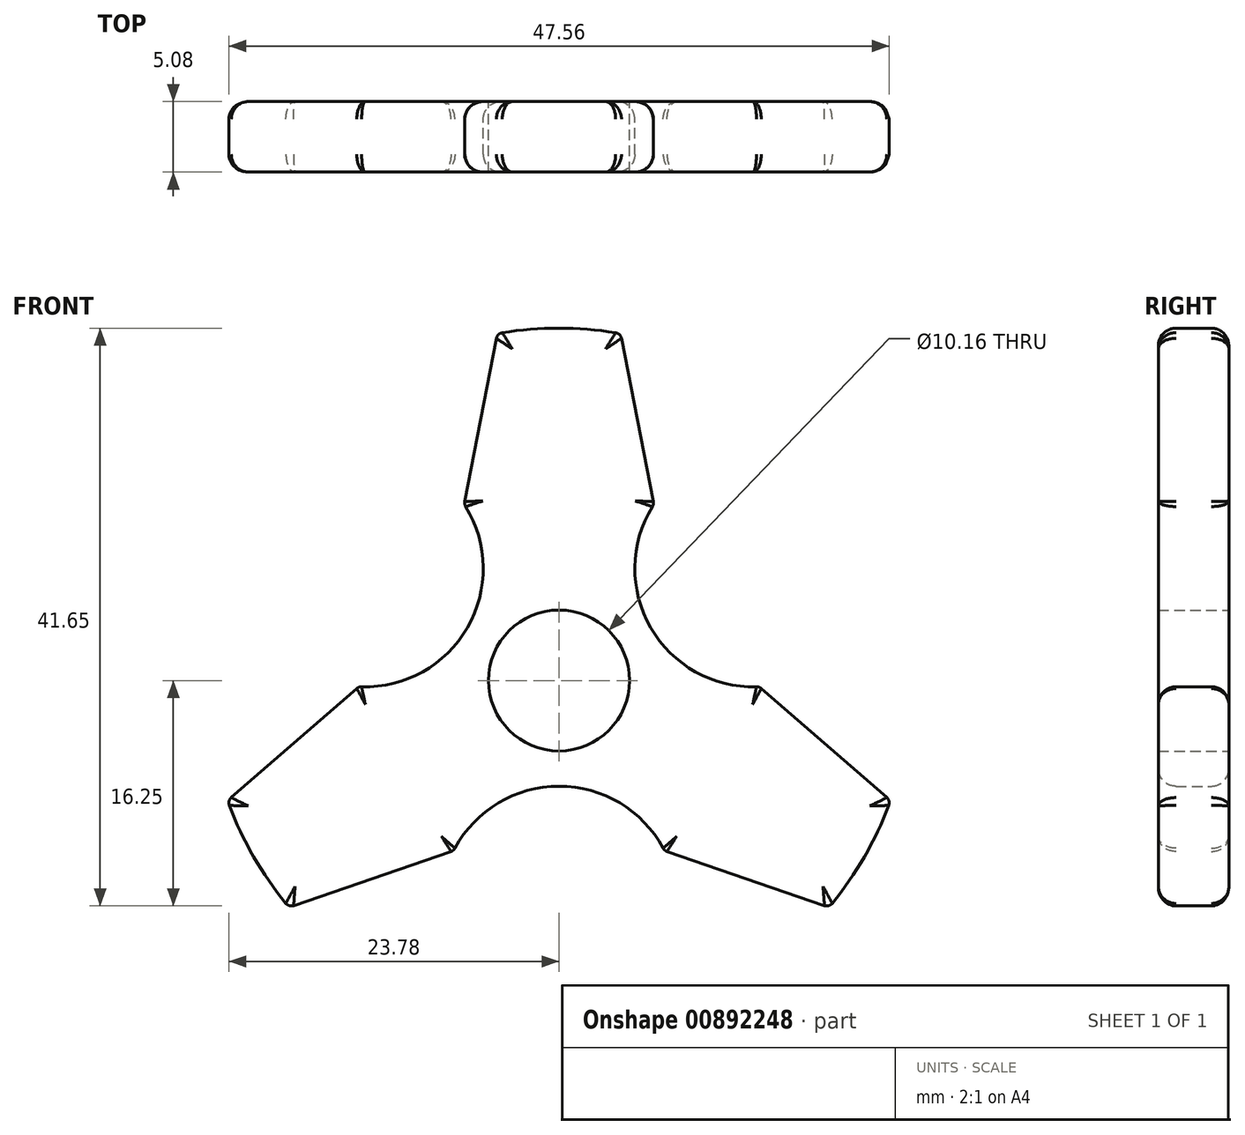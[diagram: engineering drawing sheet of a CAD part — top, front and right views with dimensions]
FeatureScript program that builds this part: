
annotation { "Feature Type Name" : "Feature", "Feature Type Description" : "" }
export const myFeature = defineFeature(function(context is Context, id is Id, definition is map)
    precondition{}
    {
        {
            var Q0;
            Q0=qCreatedBy(makeId("Front.planeOp"),FACE);
            var sketch = newSketch(context, id + "F0", { "sketchPlane" : qUnion([Q0])});
            skCircle(sketch, "E0", {"center": v(0, 0) * mm, "radius": 7.62 * mm});
            skCircle(sketch, "E1", {"center": v(0, 0) * mm, "radius": 25.4 * mm});
            skLineSegment(sketch, "E2", {"start": v(0, 25.4) * mm, "end": v(0, 0) * mm});
            skLineSegment(sketch, "E3", {"start": v(0, 0) * mm, "end": v(-22, -12.7) * mm});
            skLineSegment(sketch, "E4", {"start": v(0, 0) * mm, "end": v(22, -12.7) * mm});
            skPoint(sketch, "E5", {"position": v(-23.87, -8.67) * mm});
            skPoint(sketch, "E6", {"position": v(-19.45, -16.34) * mm});
            skPoint(sketch, "E7", {"position": v(19.45, -16.34) * mm});
            skPoint(sketch, "E8", {"position": v(23.87, -8.67) * mm});
            skPoint(sketch, "E9", {"position": v(4.43, 25.01) * mm});
            skPoint(sketch, "E10", {"position": v(-4.45, 25) * mm});
            skPoint(sketch, "E11", {"position": v(0, 7.62) * mm});
            skPoint(sketch, "E12", {"position": v(-6.6, -3.8) * mm});
            skPoint(sketch, "E13", {"position": v(6.6, -3.8) * mm});
            skLineSegment(sketch, "E14", {"start": v(0, 7.62) * mm, "end": v(-6.83, 12.7) * mm});
            skLineSegment(sketch, "E15", {"start": v(0, 7.62) * mm, "end": v(6.83, 12.7) * mm});
            skLineSegment(sketch, "E16", {"start": v(-4.44, 25) * mm, "end": v(-6.83, 12.7) * mm});
            skLineSegment(sketch, "E17", {"start": v(4.43, 25.01) * mm, "end": v(6.83, 12.7) * mm});
            skLineSegment(sketch, "E18", {"start": v(-6.6, -3.8) * mm, "end": v(-7.6, -12.26) * mm});
            skLineSegment(sketch, "E19", {"start": v(-6.6, -3.8) * mm, "end": v(-14.41, -0.44) * mm});
            skLineSegment(sketch, "E20", {"start": v(6.6, -3.8) * mm, "end": v(7.6, -12.26) * mm});
            skLineSegment(sketch, "E21", {"start": v(6.6, -3.8) * mm, "end": v(14.41, -0.44) * mm});
            skLineSegment(sketch, "E22", {"start": v(14.41, -0.44) * mm, "end": v(23.87, -8.67) * mm});
            skLineSegment(sketch, "E23", {"start": v(7.6, -12.26) * mm, "end": v(19.45, -16.34) * mm});
            skLineSegment(sketch, "E24", {"start": v(-7.6, -12.26) * mm, "end": v(-19.45, -16.34) * mm});
            skLineSegment(sketch, "E25", {"start": v(-14.41, -0.44) * mm, "end": v(-23.87, -8.67) * mm});
            skCircle(sketch, "E26", {"center": v(-13.98, 8.07) * mm, "radius": 8.52 * mm});
            skCircle(sketch, "E27", {"center": v(13.98, 8.07) * mm, "radius": 8.52 * mm});
            skCircle(sketch, "E28", {"center": v(0, -16.15) * mm, "radius": 8.53 * mm});
            skCircle(sketch, "E29", {"center": v(0, 0) * mm, "radius": 5.08 * mm});
            skSolve(sketch);
        }
        {
            var Q0;
            {var subQ4=sQuery(id+"F0.wireOp",EDGE,"E15");Q0=makeQuery(id+"F0.imprint","IMPRINT",FACE,{"disambiguationData":[TD([[makeQuery(id+"F0.imprint","IMPRINT",EDGE,{"derivedFrom":subQ4}),1.0]])]});}
            var Q1;
            {var subQ4=sQuery(id+"F0.wireOp",EDGE,"E14");Q1=makeQuery(id+"F0.imprint","IMPRINT",FACE,{"disambiguationData":[TD([[makeQuery(id+"F0.imprint","IMPRINT",EDGE,{"derivedFrom":subQ4}),-1.0]])]});}
            var Q2;
            {var subQ0=sQuery(id+"F0.wireOp",EDGE,"E14");Q2=makeQuery(id+"F0.imprint","IMPRINT",FACE,{"disambiguationData":[TD([[makeQuery(id+"F0.imprint","IMPRINT",EDGE,{"derivedFrom":subQ0}),1.0]])]});}
            var Q3;
            {var subQ0=sQuery(id+"F0.wireOp",EDGE,"E15");Q3=makeQuery(id+"F0.imprint","IMPRINT",FACE,{"disambiguationData":[TD([[makeQuery(id+"F0.imprint","IMPRINT",EDGE,{"derivedFrom":subQ0}),-1.0]])]});}
            var Q4;
            {var subQ1=sQuery(id+"F0.wireOp",EDGE,"E0");var subQ3=makeQuery(id+"F0.imprint","INTERSECT",VERTEX,{"derivedFrom":[subQ1,sQuery(id+"F0.wireOp",EDGE,"E27")]});Q4=makeQuery(id+"F0.imprint","IMPRINT",FACE,{"disambiguationData":[TD([[makeQuery(id+"F0.imprint","IMPRINT",EDGE,{"disambiguationData":[TD([[subQ3,-1.0]])],"derivedFrom":subQ1}),1.0]])]});}
            var Q5;
            {var subQ1=sQuery(id+"F0.wireOp",EDGE,"E0");var subQ3=makeQuery(id+"F0.imprint","INTERSECT",VERTEX,{"derivedFrom":[subQ1,sQuery(id+"F0.wireOp",EDGE,"E26")]});Q5=makeQuery(id+"F0.imprint","IMPRINT",FACE,{"disambiguationData":[TD([[makeQuery(id+"F0.imprint","IMPRINT",EDGE,{"disambiguationData":[TD([[subQ3,1.0]])],"derivedFrom":subQ1}),1.0]])]});}
            var Q6;
            {var subQ0=sQuery(id+"F0.wireOp",EDGE,"E19");Q6=makeQuery(id+"F0.imprint","IMPRINT",FACE,{"disambiguationData":[TD([[makeQuery(id+"F0.imprint","IMPRINT",EDGE,{"derivedFrom":subQ0}),-1.0]])]});}
            var Q7;
            {var subQ4=sQuery(id+"F0.wireOp",EDGE,"E19");Q7=makeQuery(id+"F0.imprint","IMPRINT",FACE,{"disambiguationData":[TD([[makeQuery(id+"F0.imprint","IMPRINT",EDGE,{"derivedFrom":subQ4}),1.0]])]});}
            var Q8;
            {var subQ4=sQuery(id+"F0.wireOp",EDGE,"E18");Q8=makeQuery(id+"F0.imprint","IMPRINT",FACE,{"disambiguationData":[TD([[makeQuery(id+"F0.imprint","IMPRINT",EDGE,{"derivedFrom":subQ4}),-1.0]])]});}
            var Q9;
            {var subQ0=sQuery(id+"F0.wireOp",EDGE,"E18");Q9=makeQuery(id+"F0.imprint","IMPRINT",FACE,{"disambiguationData":[TD([[makeQuery(id+"F0.imprint","IMPRINT",EDGE,{"derivedFrom":subQ0}),1.0]])]});}
            var Q10;
            {var subQ1=sQuery(id+"F0.wireOp",EDGE,"E0");var subQ3=makeQuery(id+"F0.imprint","INTERSECT",VERTEX,{"derivedFrom":[subQ1,sQuery(id+"F0.wireOp",EDGE,"E28")]});Q10=makeQuery(id+"F0.imprint","IMPRINT",FACE,{"disambiguationData":[TD([[makeQuery(id+"F0.imprint","IMPRINT",EDGE,{"disambiguationData":[TD([[subQ3,1.0]])],"derivedFrom":subQ1}),1.0]])]});}
            var Q11;
            {var subQ4=sQuery(id+"F0.wireOp",EDGE,"E20");Q11=makeQuery(id+"F0.imprint","IMPRINT",FACE,{"disambiguationData":[TD([[makeQuery(id+"F0.imprint","IMPRINT",EDGE,{"derivedFrom":subQ4}),1.0]])]});}
            var Q12;
            {var subQ0=sQuery(id+"F0.wireOp",EDGE,"E20");Q12=makeQuery(id+"F0.imprint","IMPRINT",FACE,{"disambiguationData":[TD([[makeQuery(id+"F0.imprint","IMPRINT",EDGE,{"derivedFrom":subQ0}),-1.0]])]});}
            var Q13;
            {var subQ0=sQuery(id+"F0.wireOp",EDGE,"E21");Q13=makeQuery(id+"F0.imprint","IMPRINT",FACE,{"disambiguationData":[TD([[makeQuery(id+"F0.imprint","IMPRINT",EDGE,{"derivedFrom":subQ0}),1.0]])]});}
            var Q14;
            {var subQ4=sQuery(id+"F0.wireOp",EDGE,"E21");Q14=makeQuery(id+"F0.imprint","IMPRINT",FACE,{"disambiguationData":[TD([[makeQuery(id+"F0.imprint","IMPRINT",EDGE,{"derivedFrom":subQ4}),-1.0]])]});}
            extrude(context, id + "F1", {"entities" : qUnion([Q0, Q1, Q2, Q3, Q4, Q5, Q6, Q7, Q8, Q9, Q10, Q11, Q12, Q13, Q14]), "endBound" : BoundingType.SYMMETRIC, "depth" : 5.08 * mm, "offsetDistance" : 25.4 * mm});
        }
        {
            var Q0;
            Q0=makeQuery(id+"F1.opExtrude","CAP_EDGE",EDGE,{"disambiguationData":[OSD([sQuery(id+"F0.wireOp",EDGE,"E17")])],"isStart":false});
            var Q1;
            Q1=makeQuery(id+"F1.opExtrude","CAP_EDGE",EDGE,{"disambiguationData":[OSD([sQuery(id+"F0.wireOp",EDGE,"E22")])],"isStart":false});
            var Q2;
            Q2=makeQuery(id+"F1.opExtrude","CAP_EDGE",EDGE,{"disambiguationData":[OSD([sQuery(id+"F0.wireOp",EDGE,"E27")])],"isStart":false});
            var Q3;
            Q3=makeQuery(id+"F1.opExtrude","CAP_EDGE",EDGE,{"disambiguationData":[OSD([sQuery(id+"F0.wireOp",EDGE,"E23")])],"isStart":false});
            var Q4;
            {var subQ0=sQuery(id+"F0.wireOp",EDGE,"E1");var subQ1=makeQuery(id+"F0.imprint","INTERSECT",VERTEX,{"derivedFrom":[subQ0,sQuery(id+"F0.wireOp",EDGE,"E4")]});Q4=makeQuery(id+"F1.opExtrude","CAP_EDGE",EDGE,{"disambiguationData":[OSD([subQ0]),TDD([makeQuery(id+"F0.imprint","IMPRINT",EDGE,{"disambiguationData":[TD([[subQ1,1.0]])],"derivedFrom":subQ0}),makeQuery(id+"F0.imprint","IMPRINT",EDGE,{"disambiguationData":[TD([[subQ1,-1.0]])],"derivedFrom":subQ0})])],"isStart":false});}
            var Q5;
            Q5=makeQuery(id+"F1.opExtrude","CAP_EDGE",EDGE,{"disambiguationData":[OSD([sQuery(id+"F0.wireOp",EDGE,"E28")])],"isStart":false});
            var Q6;
            Q6=makeQuery(id+"F1.opExtrude","CAP_EDGE",EDGE,{"disambiguationData":[OSD([sQuery(id+"F0.wireOp",EDGE,"E24")])],"isStart":false});
            var Q7;
            {var subQ0=sQuery(id+"F0.wireOp",EDGE,"E1");var subQ1=makeQuery(id+"F0.imprint","INTERSECT",VERTEX,{"derivedFrom":[subQ0,sQuery(id+"F0.wireOp",EDGE,"E3")]});Q7=makeQuery(id+"F1.opExtrude","CAP_EDGE",EDGE,{"disambiguationData":[OSD([subQ0]),TDD([makeQuery(id+"F0.imprint","IMPRINT",EDGE,{"disambiguationData":[TD([[subQ1,1.0]])],"derivedFrom":subQ0}),makeQuery(id+"F0.imprint","IMPRINT",EDGE,{"disambiguationData":[TD([[subQ1,-1.0]])],"derivedFrom":subQ0})])],"isStart":false});}
            var Q8;
            Q8=makeQuery(id+"F1.opExtrude","CAP_EDGE",EDGE,{"disambiguationData":[OSD([sQuery(id+"F0.wireOp",EDGE,"E25")])],"isStart":false});
            var Q9;
            Q9=makeQuery(id+"F1.opExtrude","CAP_EDGE",EDGE,{"disambiguationData":[OSD([sQuery(id+"F0.wireOp",EDGE,"E26")])],"isStart":false});
            var Q10;
            Q10=makeQuery(id+"F1.opExtrude","CAP_EDGE",EDGE,{"disambiguationData":[OSD([sQuery(id+"F0.wireOp",EDGE,"E16")])],"isStart":false});
            var Q11;
            {var subQ0=sQuery(id+"F0.wireOp",EDGE,"E1");var subQ1=makeQuery(id+"F0.imprint","INTERSECT",VERTEX,{"derivedFrom":[subQ0,sQuery(id+"F0.wireOp",EDGE,"E2")]});Q11=makeQuery(id+"F1.opExtrude","CAP_EDGE",EDGE,{"disambiguationData":[OSD([subQ0]),TDD([makeQuery(id+"F0.imprint","IMPRINT",EDGE,{"disambiguationData":[TD([[subQ1,1.0]])],"derivedFrom":subQ0}),makeQuery(id+"F0.imprint","IMPRINT",EDGE,{"disambiguationData":[TD([[subQ1,-1.0]])],"derivedFrom":subQ0})])],"isStart":false});}
            fillet(context, id + "F2", {"entities" : qUnion([Q0, Q1, Q2, Q3, Q4, Q5, Q6, Q7, Q8, Q9, Q10, Q11]), "radius" : 1.27 * mm, "tangentPropagation" : true, "allowEdgeOverflow" : false});
        }
        {
            var Q0;
            Q0=makeQuery(id+"F1.opExtrude","CAP_EDGE",EDGE,{"disambiguationData":[OSD([sQuery(id+"F0.wireOp",EDGE,"E24")])],"isStart":true});
            var Q1;
            Q1=makeQuery(id+"F1.opExtrude","CAP_EDGE",EDGE,{"disambiguationData":[OSD([sQuery(id+"F0.wireOp",EDGE,"E28")])],"isStart":true});
            var Q2;
            Q2=makeQuery(id+"F1.opExtrude","CAP_EDGE",EDGE,{"disambiguationData":[OSD([sQuery(id+"F0.wireOp",EDGE,"E23")])],"isStart":true});
            var Q3;
            {var subQ0=sQuery(id+"F0.wireOp",EDGE,"E1");var subQ1=makeQuery(id+"F0.imprint","INTERSECT",VERTEX,{"derivedFrom":[subQ0,sQuery(id+"F0.wireOp",EDGE,"E4")]});Q3=makeQuery(id+"F1.opExtrude","CAP_EDGE",EDGE,{"disambiguationData":[OSD([subQ0]),TDD([makeQuery(id+"F0.imprint","IMPRINT",EDGE,{"disambiguationData":[TD([[subQ1,1.0]])],"derivedFrom":subQ0}),makeQuery(id+"F0.imprint","IMPRINT",EDGE,{"disambiguationData":[TD([[subQ1,-1.0]])],"derivedFrom":subQ0})])],"isStart":true});}
            var Q4;
            Q4=makeQuery(id+"F1.opExtrude","CAP_EDGE",EDGE,{"disambiguationData":[OSD([sQuery(id+"F0.wireOp",EDGE,"E22")])],"isStart":true});
            var Q5;
            Q5=makeQuery(id+"F1.opExtrude","CAP_EDGE",EDGE,{"disambiguationData":[OSD([sQuery(id+"F0.wireOp",EDGE,"E27")])],"isStart":true});
            var Q6;
            Q6=makeQuery(id+"F1.opExtrude","CAP_EDGE",EDGE,{"disambiguationData":[OSD([sQuery(id+"F0.wireOp",EDGE,"E17")])],"isStart":true});
            var Q7;
            {var subQ0=sQuery(id+"F0.wireOp",EDGE,"E1");var subQ1=makeQuery(id+"F0.imprint","INTERSECT",VERTEX,{"derivedFrom":[subQ0,sQuery(id+"F0.wireOp",EDGE,"E2")]});Q7=makeQuery(id+"F1.opExtrude","CAP_EDGE",EDGE,{"disambiguationData":[OSD([subQ0]),TDD([makeQuery(id+"F0.imprint","IMPRINT",EDGE,{"disambiguationData":[TD([[subQ1,1.0]])],"derivedFrom":subQ0}),makeQuery(id+"F0.imprint","IMPRINT",EDGE,{"disambiguationData":[TD([[subQ1,-1.0]])],"derivedFrom":subQ0})])],"isStart":true});}
            var Q8;
            Q8=makeQuery(id+"F1.opExtrude","CAP_EDGE",EDGE,{"disambiguationData":[OSD([sQuery(id+"F0.wireOp",EDGE,"E16")])],"isStart":true});
            var Q9;
            Q9=makeQuery(id+"F1.opExtrude","CAP_EDGE",EDGE,{"disambiguationData":[OSD([sQuery(id+"F0.wireOp",EDGE,"E26")])],"isStart":true});
            var Q10;
            Q10=makeQuery(id+"F1.opExtrude","CAP_EDGE",EDGE,{"disambiguationData":[OSD([sQuery(id+"F0.wireOp",EDGE,"E25")])],"isStart":true});
            var Q11;
            {var subQ0=sQuery(id+"F0.wireOp",EDGE,"E1");var subQ1=makeQuery(id+"F0.imprint","INTERSECT",VERTEX,{"derivedFrom":[subQ0,sQuery(id+"F0.wireOp",EDGE,"E3")]});Q11=makeQuery(id+"F1.opExtrude","CAP_EDGE",EDGE,{"disambiguationData":[OSD([subQ0]),TDD([makeQuery(id+"F0.imprint","IMPRINT",EDGE,{"disambiguationData":[TD([[subQ1,1.0]])],"derivedFrom":subQ0}),makeQuery(id+"F0.imprint","IMPRINT",EDGE,{"disambiguationData":[TD([[subQ1,-1.0]])],"derivedFrom":subQ0})])],"isStart":true});}
            fillet(context, id + "F3", {"entities" : qUnion([Q0, Q1, Q2, Q3, Q4, Q5, Q6, Q7, Q8, Q9, Q10, Q11]), "radius" : 1.27 * mm, "tangentPropagation" : true, "allowEdgeOverflow" : false});
        }
        {
            var Q0;
            Q0=makeQuery(id+"F1.opExtrude","SWEPT_EDGE",EDGE,{"disambiguationData":[OSD([sQuery(id+"F0.wireOp",EDGE,"E1"),sQuery(id+"F0.wireOp",EDGE,"E16")])]});
            var Q1;
            Q1=makeQuery(id+"F1.opExtrude","SWEPT_EDGE",EDGE,{"disambiguationData":[OSD([sQuery(id+"F0.wireOp",EDGE,"E14"),sQuery(id+"F0.wireOp",EDGE,"E16"),sQuery(id+"F0.wireOp",EDGE,"E26")])]});
            var Q2;
            Q2=makeQuery(id+"F1.opExtrude","SWEPT_EDGE",EDGE,{"disambiguationData":[OSD([sQuery(id+"F0.wireOp",EDGE,"E1"),sQuery(id+"F0.wireOp",EDGE,"E17")])]});
            var Q3;
            Q3=makeQuery(id+"F1.opExtrude","SWEPT_EDGE",EDGE,{"disambiguationData":[OSD([sQuery(id+"F0.wireOp",EDGE,"E15"),sQuery(id+"F0.wireOp",EDGE,"E17"),sQuery(id+"F0.wireOp",EDGE,"E27")])]});
            var Q4;
            Q4=makeQuery(id+"F1.opExtrude","SWEPT_EDGE",EDGE,{"disambiguationData":[OSD([sQuery(id+"F0.wireOp",EDGE,"E19"),sQuery(id+"F0.wireOp",EDGE,"E25"),sQuery(id+"F0.wireOp",EDGE,"E26")])]});
            var Q5;
            Q5=makeQuery(id+"F1.opExtrude","SWEPT_EDGE",EDGE,{"disambiguationData":[OSD([sQuery(id+"F0.wireOp",EDGE,"E1"),sQuery(id+"F0.wireOp",EDGE,"E25")])]});
            var Q6;
            Q6=makeQuery(id+"F1.opExtrude","SWEPT_EDGE",EDGE,{"disambiguationData":[OSD([sQuery(id+"F0.wireOp",EDGE,"E1"),sQuery(id+"F0.wireOp",EDGE,"E24")])]});
            var Q7;
            Q7=makeQuery(id+"F1.opExtrude","SWEPT_EDGE",EDGE,{"disambiguationData":[OSD([sQuery(id+"F0.wireOp",EDGE,"E18"),sQuery(id+"F0.wireOp",EDGE,"E24"),sQuery(id+"F0.wireOp",EDGE,"E28")])]});
            var Q8;
            Q8=makeQuery(id+"F1.opExtrude","SWEPT_EDGE",EDGE,{"disambiguationData":[OSD([sQuery(id+"F0.wireOp",EDGE,"E1"),sQuery(id+"F0.wireOp",EDGE,"E23")])]});
            var Q9;
            Q9=makeQuery(id+"F1.opExtrude","SWEPT_EDGE",EDGE,{"disambiguationData":[OSD([sQuery(id+"F0.wireOp",EDGE,"E20"),sQuery(id+"F0.wireOp",EDGE,"E23"),sQuery(id+"F0.wireOp",EDGE,"E28")])]});
            var Q10;
            Q10=makeQuery(id+"F1.opExtrude","SWEPT_EDGE",EDGE,{"disambiguationData":[OSD([sQuery(id+"F0.wireOp",EDGE,"E1"),sQuery(id+"F0.wireOp",EDGE,"E22")])]});
            var Q11;
            Q11=makeQuery(id+"F1.opExtrude","SWEPT_EDGE",EDGE,{"disambiguationData":[OSD([sQuery(id+"F0.wireOp",EDGE,"E21"),sQuery(id+"F0.wireOp",EDGE,"E22"),sQuery(id+"F0.wireOp",EDGE,"E27")])]});
            fillet(context, id + "F4", {"entities" : qUnion([Q0, Q1, Q2, Q3, Q4, Q5, Q6, Q7, Q8, Q9, Q10, Q11]), "radius" : 0.5 * mm, "tangentPropagation" : true, "allowEdgeOverflow" : false});
        }
    });
